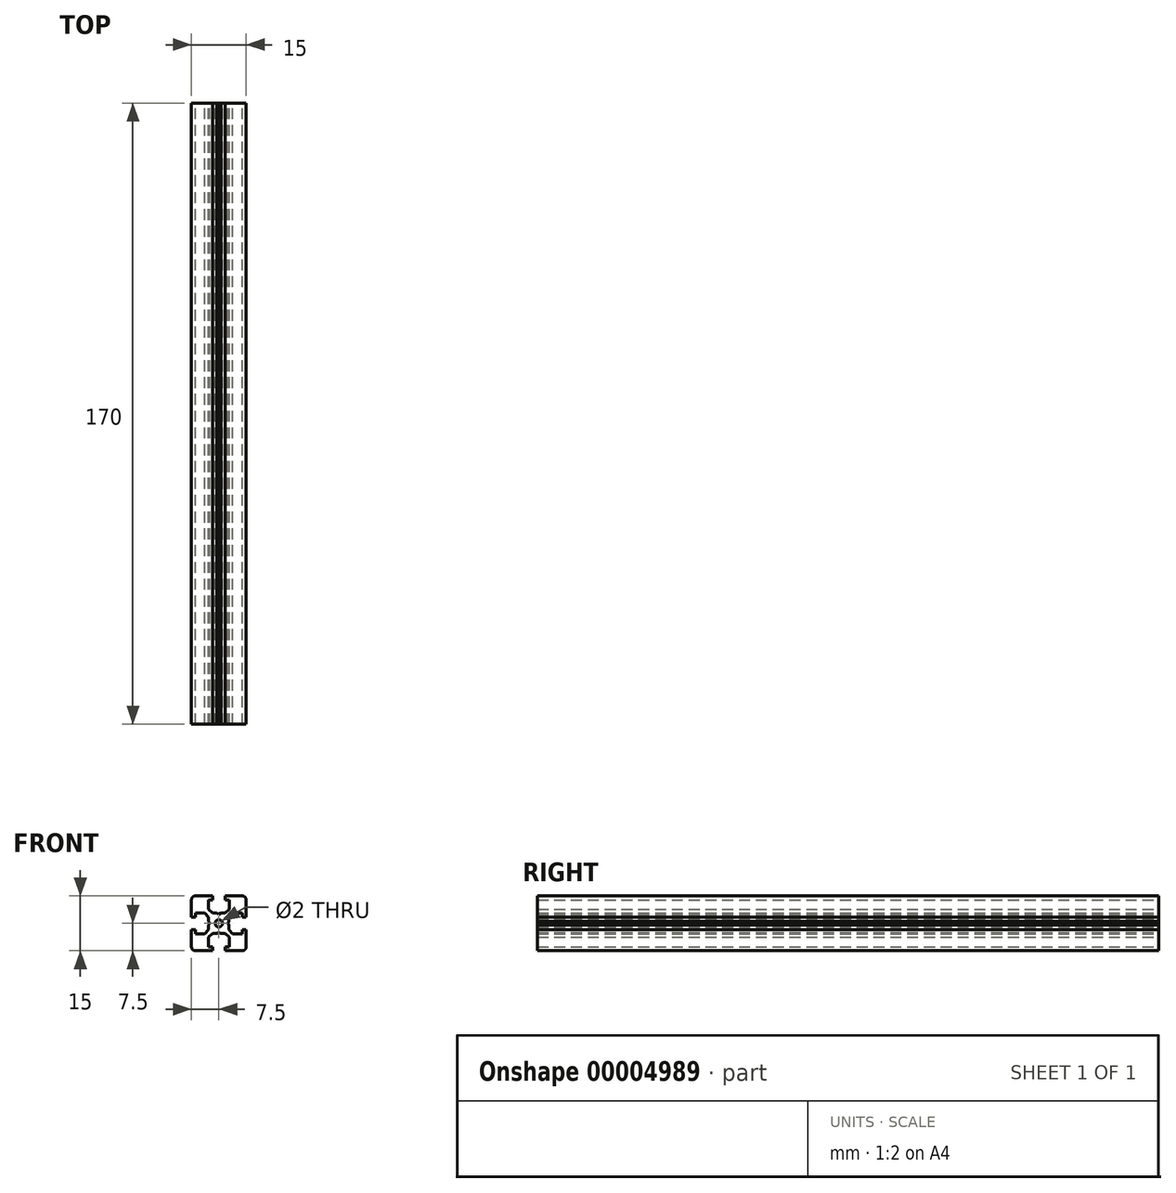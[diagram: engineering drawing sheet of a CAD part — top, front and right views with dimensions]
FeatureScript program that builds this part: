
annotation { "Feature Type Name" : "Feature", "Feature Type Description" : "" }
export const myFeature = defineFeature(function(context is Context, id is Id, definition is map)
    precondition{}
    {
        {
            var Q0;
            Q0=qCreatedBy(makeId("Front.planeOp"),FACE);
            var sketch = newSketch(context, id + "F0", { "sketchPlane" : qUnion([Q0])});
            skCircle(sketch, "E0", {"center": v(0, 0) * mm, "radius": 1 * mm});
            skLineSegment(sketch, "E1.bottom", {"start": v(0, 0) * mm, "end": v(-7.5, 0) * mm, "construction": true});
            skLineSegment(sketch, "E1.top", {"start": v(0, 7.5) * mm, "end": v(-7.5, 7.5) * mm, "construction": true});
            skLineSegment(sketch, "E1.left", {"start": v(0, 0) * mm, "end": v(0, 7.5) * mm, "construction": true});
            skLineSegment(sketch, "E1.right", {"start": v(-7.5, 0) * mm, "end": v(-7.5, 7.5) * mm, "construction": true});
            skLineSegment(sketch, "E2", {"start": v(-2.85, 3.8) * mm, "end": v(-1.7, 2.8) * mm});
            skLineSegment(sketch, "E3", {"start": v(-1.7, 2.8) * mm, "end": v(-0.52, 2.8) * mm});
            skLineSegment(sketch, "E4", {"start": v(-0.52, 2.8) * mm, "end": v(0, 2.5) * mm});
            skLineSegment(sketch, "E5", {"start": v(-7.5, 7.5) * mm, "end": v(-1.7, 7.5) * mm});
            skLineSegment(sketch, "E6", {"start": v(-1.7, 7.5) * mm, "end": v(-1.7, 6.4) * mm});
            skLineSegment(sketch, "E7", {"start": v(-1.7, 6.4) * mm, "end": v(-2.85, 6.4) * mm});
            skLineSegment(sketch, "E8", {"start": v(-2.85, 6.4) * mm, "end": v(-2.85, 3.8) * mm});
            skLineSegment(sketch, "E9", {"start": v(-7.5, 7.5) * mm, "end": v(0, 0) * mm, "construction": true});
            skLineSegment(sketch, "E10.0.MirrorCS", {"start": v(-2.8, 0.52) * mm, "end": v(-2.5, 0) * mm});
            skLineSegment(sketch, "E10.1.MirrorCS", {"start": v(-2.8, 1.7) * mm, "end": v(-2.8, 0.52) * mm});
            skLineSegment(sketch, "E10.2.MirrorCS", {"start": v(-3.8, 2.85) * mm, "end": v(-2.8, 1.7) * mm});
            skLineSegment(sketch, "E10.3.MirrorCS", {"start": v(-6.4, 2.85) * mm, "end": v(-3.8, 2.85) * mm});
            skLineSegment(sketch, "E10.4.MirrorCS", {"start": v(-6.4, 1.7) * mm, "end": v(-6.4, 2.85) * mm});
            skLineSegment(sketch, "E10.5.MirrorCS", {"start": v(-7.5, 1.7) * mm, "end": v(-6.4, 1.7) * mm});
            skLineSegment(sketch, "E10.6.MirrorCS", {"start": v(-7.5, 7.5) * mm, "end": v(-7.5, 1.7) * mm});
            skLineSegment(sketch, "E11.0.MirrorCS", {"start": v(2.8, 0.52) * mm, "end": v(2.5, 0) * mm});
            skLineSegment(sketch, "E11.1.MirrorCS", {"start": v(2.8, 1.7) * mm, "end": v(2.8, 0.52) * mm});
            skLineSegment(sketch, "E11.2.MirrorCS", {"start": v(3.8, 2.85) * mm, "end": v(2.8, 1.7) * mm});
            skLineSegment(sketch, "E11.3.MirrorCS", {"start": v(6.4, 2.85) * mm, "end": v(3.8, 2.85) * mm});
            skLineSegment(sketch, "E11.4.MirrorCS", {"start": v(6.4, 1.7) * mm, "end": v(6.4, 2.85) * mm});
            skLineSegment(sketch, "E11.5.MirrorCS", {"start": v(7.5, 1.7) * mm, "end": v(6.4, 1.7) * mm});
            skLineSegment(sketch, "E11.6.MirrorCS", {"start": v(7.5, 7.5) * mm, "end": v(7.5, 1.7) * mm});
            skLineSegment(sketch, "E11.7.MirrorCS", {"start": v(7.5, 7.5) * mm, "end": v(1.7, 7.5) * mm});
            skLineSegment(sketch, "E11.8.MirrorCS", {"start": v(1.7, 7.5) * mm, "end": v(1.7, 6.4) * mm});
            skLineSegment(sketch, "E11.9.MirrorCS", {"start": v(1.7, 6.4) * mm, "end": v(2.85, 6.4) * mm});
            skLineSegment(sketch, "E11.10.MirrorCS", {"start": v(2.85, 6.4) * mm, "end": v(2.85, 3.8) * mm});
            skLineSegment(sketch, "E11.11.MirrorCS", {"start": v(2.85, 3.8) * mm, "end": v(1.7, 2.8) * mm});
            skLineSegment(sketch, "E11.12.MirrorCS", {"start": v(1.7, 2.8) * mm, "end": v(0.52, 2.8) * mm});
            skLineSegment(sketch, "E11.13.MirrorCS", {"start": v(0.52, 2.8) * mm, "end": v(0, 2.5) * mm});
            skLineSegment(sketch, "E12.0.MirrorCS", {"start": v(2.8, -0.52) * mm, "end": v(2.5, 0) * mm});
            skLineSegment(sketch, "E12.1.MirrorCS", {"start": v(2.8, -1.7) * mm, "end": v(2.8, -0.52) * mm});
            skLineSegment(sketch, "E12.2.MirrorCS", {"start": v(3.8, -2.85) * mm, "end": v(2.8, -1.7) * mm});
            skLineSegment(sketch, "E12.3.MirrorCS", {"start": v(6.4, -2.85) * mm, "end": v(3.8, -2.85) * mm});
            skLineSegment(sketch, "E12.4.MirrorCS", {"start": v(6.4, -1.7) * mm, "end": v(6.4, -2.85) * mm});
            skLineSegment(sketch, "E12.5.MirrorCS", {"start": v(7.5, -1.7) * mm, "end": v(6.4, -1.7) * mm});
            skLineSegment(sketch, "E12.6.MirrorCS", {"start": v(7.5, -7.5) * mm, "end": v(7.5, -1.7) * mm});
            skLineSegment(sketch, "E12.7.MirrorCS", {"start": v(7.5, -7.5) * mm, "end": v(1.7, -7.5) * mm});
            skLineSegment(sketch, "E12.8.MirrorCS", {"start": v(1.7, -7.5) * mm, "end": v(1.7, -6.4) * mm});
            skLineSegment(sketch, "E12.9.MirrorCS", {"start": v(1.7, -6.4) * mm, "end": v(2.85, -6.4) * mm});
            skLineSegment(sketch, "E12.10.MirrorCS", {"start": v(2.85, -6.4) * mm, "end": v(2.85, -3.8) * mm});
            skLineSegment(sketch, "E12.11.MirrorCS", {"start": v(2.85, -3.8) * mm, "end": v(1.7, -2.8) * mm});
            skLineSegment(sketch, "E12.12.MirrorCS", {"start": v(1.7, -2.8) * mm, "end": v(0.52, -2.8) * mm});
            skLineSegment(sketch, "E12.13.MirrorCS", {"start": v(0.52, -2.8) * mm, "end": v(0, -2.5) * mm});
            skLineSegment(sketch, "E12.14.MirrorCS", {"start": v(-0.52, -2.8) * mm, "end": v(0, -2.5) * mm});
            skLineSegment(sketch, "E12.15.MirrorCS", {"start": v(-1.7, -2.8) * mm, "end": v(-0.52, -2.8) * mm});
            skLineSegment(sketch, "E12.16.MirrorCS", {"start": v(-2.85, -3.8) * mm, "end": v(-1.7, -2.8) * mm});
            skLineSegment(sketch, "E12.17.MirrorCS", {"start": v(-2.85, -6.4) * mm, "end": v(-2.85, -3.8) * mm});
            skLineSegment(sketch, "E12.18.MirrorCS", {"start": v(-1.7, -6.4) * mm, "end": v(-2.85, -6.4) * mm});
            skLineSegment(sketch, "E12.19.MirrorCS", {"start": v(-1.7, -7.5) * mm, "end": v(-1.7, -6.4) * mm});
            skLineSegment(sketch, "E12.20.MirrorCS", {"start": v(-7.5, -7.5) * mm, "end": v(-1.7, -7.5) * mm});
            skLineSegment(sketch, "E12.21.MirrorCS", {"start": v(-7.5, -7.5) * mm, "end": v(-7.5, -1.7) * mm});
            skLineSegment(sketch, "E12.22.MirrorCS", {"start": v(-7.5, -1.7) * mm, "end": v(-6.4, -1.7) * mm});
            skLineSegment(sketch, "E12.23.MirrorCS", {"start": v(-6.4, -1.7) * mm, "end": v(-6.4, -2.85) * mm});
            skLineSegment(sketch, "E12.24.MirrorCS", {"start": v(-6.4, -2.85) * mm, "end": v(-3.8, -2.85) * mm});
            skLineSegment(sketch, "E12.25.MirrorCS", {"start": v(-3.8, -2.85) * mm, "end": v(-2.8, -1.7) * mm});
            skLineSegment(sketch, "E12.26.MirrorCS", {"start": v(-2.8, -1.7) * mm, "end": v(-2.8, -0.52) * mm});
            skLineSegment(sketch, "E12.27.MirrorCS", {"start": v(-2.8, -0.52) * mm, "end": v(-2.5, 0) * mm});
            skSolve(sketch);
        }
        {
            var Q0;
            Q0 = qSketchRegion(id + "F0", true);
            extrude(context, id + "F1", {"entities" : qUnion([Q0]), "depth" : 170 * mm, "symmetric" : true});
        }
        {
            var Q0;
            Q0=makeQuery(id+"F1.opExtrude","SWEPT_EDGE",EDGE,{"disambiguationData":[OSD([sQuery(id+"F0.wireOp",EDGE,"E11.6.MirrorCS"),sQuery(id+"F0.wireOp",EDGE,"E11.7.MirrorCS")])]});
            var Q1;
            Q1=makeQuery(id+"F1.opExtrude","SWEPT_EDGE",EDGE,{"disambiguationData":[OSD([sQuery(id+"F0.wireOp",EDGE,"E5"),sQuery(id+"F0.wireOp",EDGE,"E10.6.MirrorCS")])]});
            var Q2;
            Q2=makeQuery(id+"F1.opExtrude","SWEPT_EDGE",EDGE,{"disambiguationData":[OSD([sQuery(id+"F0.wireOp",EDGE,"E12.6.MirrorCS"),sQuery(id+"F0.wireOp",EDGE,"E12.7.MirrorCS")])]});
            var Q3;
            Q3=makeQuery(id+"F1.opExtrude","SWEPT_EDGE",EDGE,{"disambiguationData":[OSD([sQuery(id+"F0.wireOp",EDGE,"E12.20.MirrorCS"),sQuery(id+"F0.wireOp",EDGE,"E12.21.MirrorCS")])]});
            fillet(context, id + "F2", {"entities" : qUnion([Q0, Q1, Q2, Q3]), "radius" : 1.1 * mm, "tangentPropagation" : true, "allowEdgeOverflow" : false});
        }
    });
